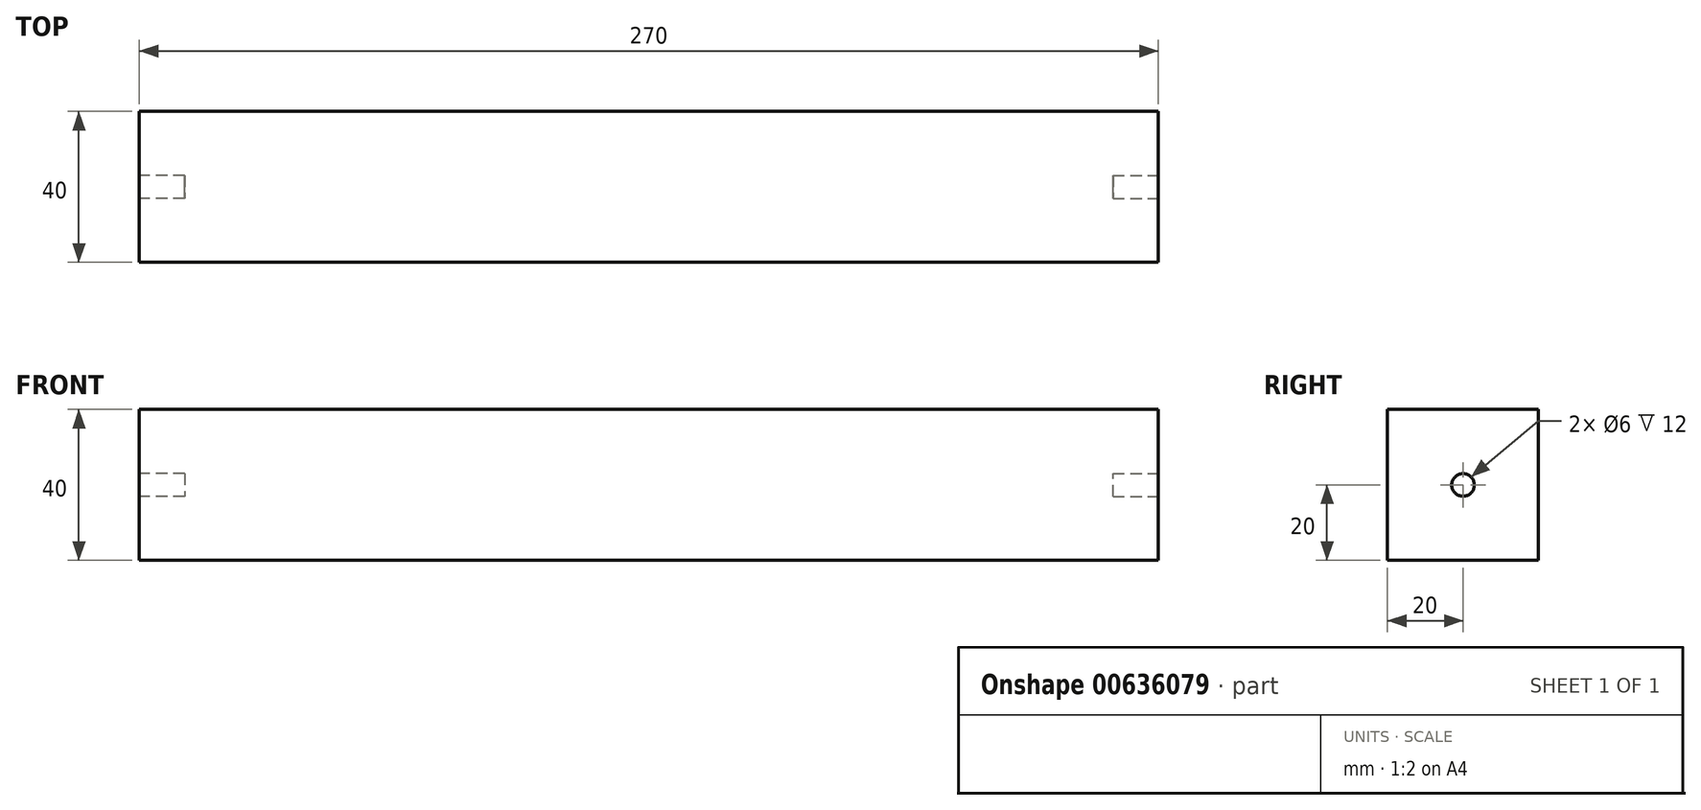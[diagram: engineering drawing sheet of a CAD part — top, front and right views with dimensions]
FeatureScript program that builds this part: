
annotation { "Feature Type Name" : "Feature", "Feature Type Description" : "" }
export const myFeature = defineFeature(function(context is Context, id is Id, definition is map)
    precondition{}
    {
        {
            var Q0;
            Q0=qCreatedBy(makeId("Right.planeOp"),FACE);
            var sketch = newSketch(context, id + "F0", { "sketchPlane" : qUnion([Q0])});
            skLineSegment(sketch, "E0.bottom", {"start": v(0, 0) * mm, "end": v(40, 0) * mm});
            skLineSegment(sketch, "E0.top", {"start": v(0, 40) * mm, "end": v(40, 40) * mm});
            skLineSegment(sketch, "E0.left", {"start": v(0, 0) * mm, "end": v(0, 40) * mm});
            skLineSegment(sketch, "E0.right", {"start": v(40, 0) * mm, "end": v(40, 40) * mm});
            skSolve(sketch);
        }
        {
            var Q0;
            Q0 = qSketchRegion(id + "F0", true);
            extrude(context, id + "F1", {"entities" : qUnion([Q0]), "depth" : 270 * mm, "offsetDistance" : 25 * mm});
        }
        {
            var Q0;
            Q0=makeQuery(id+"F1.opExtrude","CAP_FACE",FACE,{"disambiguationData":[OSD([sQuery(id+"F0.wireOp",EDGE,"E0.bottom"),sQuery(id+"F0.wireOp",EDGE,"E0.top"),sQuery(id+"F0.wireOp",EDGE,"E0.left"),sQuery(id+"F0.wireOp",EDGE,"E0.right")])],"isStart":false});
            var sketch = newSketch(context, id + "F2", { "sketchPlane" : qUnion([Q0])});
            skCircle(sketch, "E1", {"center": v(20, 20) * mm, "radius": 3 * mm});
            skSolve(sketch);
        }
        {
            var Q0;
            Q0 = qSketchRegion(id + "F2", true);
            extrude(context, id + "F3", {"entities" : qUnion([Q0]), "operationType" : NewBodyOperationType.REMOVE, "oppositeDirection" : true, "depth" : 12 * mm, "offsetDistance" : 25 * mm});
        }
        {
            var Q0;
            Q0=makeQuery(id+"F1.opExtrude","CAP_FACE",FACE,{"disambiguationData":[OSD([sQuery(id+"F0.wireOp",EDGE,"E0.bottom"),sQuery(id+"F0.wireOp",EDGE,"E0.top"),sQuery(id+"F0.wireOp",EDGE,"E0.left"),sQuery(id+"F0.wireOp",EDGE,"E0.right")])],"isStart":true});
            var sketch = newSketch(context, id + "F4", { "sketchPlane" : qUnion([Q0])});
            skCircle(sketch, "E2", {"center": v(-20, 20) * mm, "radius": 3 * mm});
            skSolve(sketch);
        }
        {
            var Q0;
            Q0 = qSketchRegion(id + "F4", true);
            extrude(context, id + "F5", {"entities" : qUnion([Q0]), "operationType" : NewBodyOperationType.REMOVE, "oppositeDirection" : true, "depth" : 12 * mm, "offsetDistance" : 25 * mm});
        }
    });
